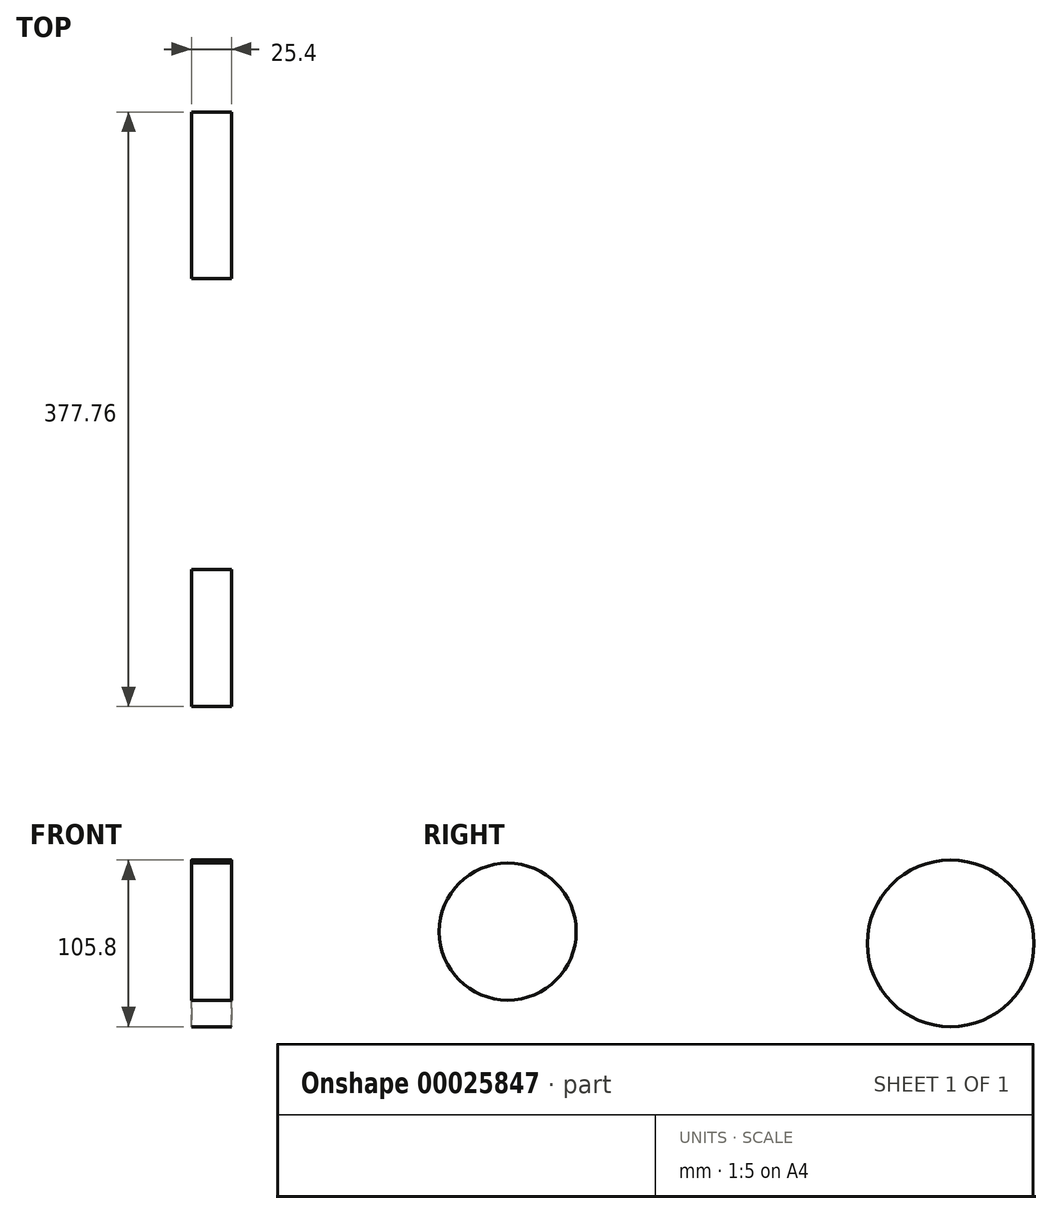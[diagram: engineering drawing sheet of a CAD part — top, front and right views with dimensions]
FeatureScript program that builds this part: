
annotation { "Feature Type Name" : "Feature", "Feature Type Description" : "" }
export const myFeature = defineFeature(function(context is Context, id is Id, definition is map)
    precondition{}
    {
        {
            var Q0;
            Q0=qCreatedBy(makeId("Right.planeOp"),FACE);
            var sketch = newSketch(context, id + "F0", { "sketchPlane" : qUnion([Q0])});
            skCircle(sketch, "E0", {"center": v(-24.22, 24.92) * mm, "radius": 52.9 * mm});
            skCircle(sketch, "E1", {"center": v(-305.56, 32.37) * mm, "radius": 43.52 * mm});
            skSolve(sketch);
        }
        {
            var Q0;
            Q0=makeQuery(id+"F0.imprint","IMPRINT",FACE,{"disambiguationData":[TD([[makeQuery(id+"F0.imprint","IMPRINT",EDGE,{"derivedFrom":sQuery(id+"F0.wireOp",EDGE,"E0")}),1.0]])]});
            var Q1;
            Q1=makeQuery(id+"F0.imprint","IMPRINT",FACE,{"disambiguationData":[TD([[makeQuery(id+"F0.imprint","IMPRINT",EDGE,{"derivedFrom":sQuery(id+"F0.wireOp",EDGE,"E1")}),1.0]])]});
            extrude(context, id + "F1", {"entities" : qUnion([Q0, Q1]), "depth" : 25.4 * mm});
        }
    });
